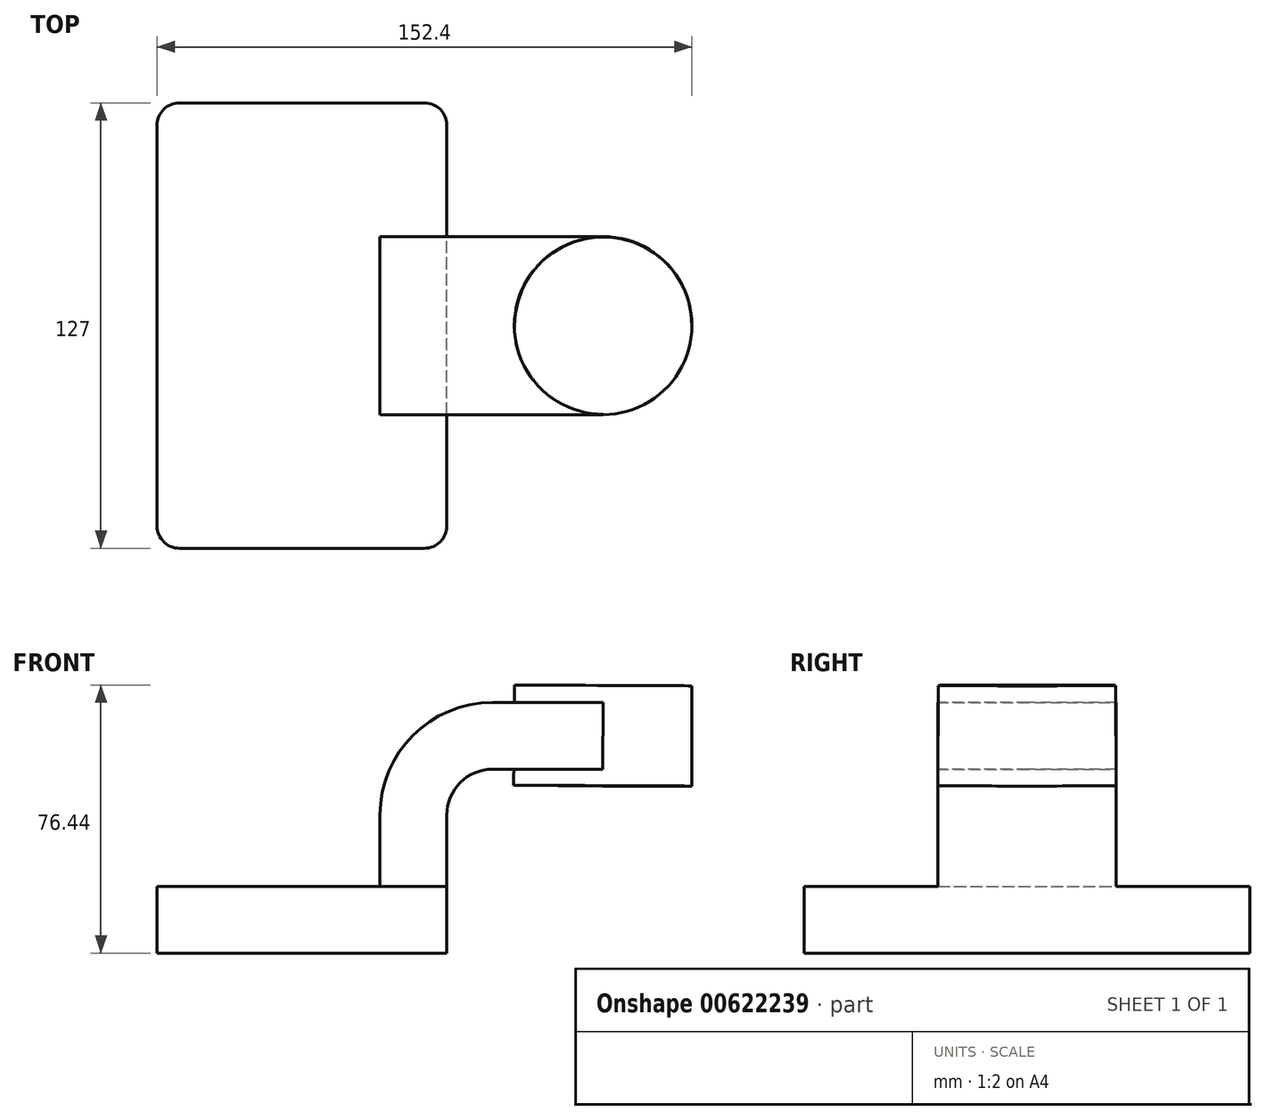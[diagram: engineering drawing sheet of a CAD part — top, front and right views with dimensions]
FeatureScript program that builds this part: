
annotation { "Feature Type Name" : "Feature", "Feature Type Description" : "" }
export const myFeature = defineFeature(function(context is Context, id is Id, definition is map)
    precondition{}
    {
        {
            var Q0;
            Q0=qCreatedBy(makeId("Front.planeOp"),FACE);
            var sketch = newSketch(context, id + "F0", { "sketchPlane" : qUnion([Q0])});
            skLineSegment(sketch, "E0.bottom", {"start": v(41.27, 9.53) * mm, "end": v(-41.28, 9.53) * mm});
            skLineSegment(sketch, "E0.top", {"start": v(41.28, -9.52) * mm, "end": v(-41.27, -9.52) * mm});
            skLineSegment(sketch, "E0.left", {"start": v(41.28, 9.53) * mm, "end": v(41.28, -9.52) * mm});
            skLineSegment(sketch, "E0.right", {"start": v(-41.28, 9.53) * mm, "end": v(-41.27, -9.52) * mm});
            skPoint(sketch, "E0.middle", {"position": v(0, 0) * mm});
            skLineSegment(sketch, "E1.bottom", {"start": v(111.12, 66.68) * mm, "end": v(60.32, 66.68) * mm});
            skLineSegment(sketch, "E1.top", {"start": v(111.12, 38.1) * mm, "end": v(60.32, 38.1) * mm});
            skLineSegment(sketch, "E1.left", {"start": v(111.12, 66.68) * mm, "end": v(111.12, 38.1) * mm});
            skLineSegment(sketch, "E1.right", {"start": v(60.32, 66.68) * mm, "end": v(60.32, 38.1) * mm});
            skPoint(sketch, "E1.middle", {"position": v(85.72, 52.39) * mm});
            skLineSegment(sketch, "E2", {"start": v(41.27, 9.53) * mm, "end": v(41.27, 29.84) * mm});
            skArc(sketch, "E3", {"start": v(41.27, 29.84) * mm, "mid": v(45.1, 39.06) * mm, "end": v(54.31, 42.88) * mm});
            skLineSegment(sketch, "E4", {"start": v(54.31, 42.88) * mm, "end": v(85.86, 42.88) * mm});
            skLineSegment(sketch, "E5.0", {"start": v(54.31, 61.93) * mm, "end": v(85.86, 61.93) * mm});
            skArc(sketch, "E5.1", {"start": v(22.22, 29.84) * mm, "mid": v(31.62, 52.53) * mm, "end": v(54.31, 61.93) * mm});
            skLineSegment(sketch, "E5.2", {"start": v(22.22, 9.53) * mm, "end": v(22.22, 29.84) * mm});
            skLineSegment(sketch, "E6", {"start": v(85.72, 38.1) * mm, "end": v(85.86, 66.68) * mm});
            skFitSpline(sketch, "E7", {"points": [v(-41.28, 9.52) * mm, v(54.31, 61.93) * mm], "startDerivative": vector(4.7, 92.75) * mm, "endDerivative": vector(132.26, -2.13) * mm});
            skSolve(sketch);
        }
        {
            var Q0;
            Q0=makeQuery(id+"F0.imprint","IMPRINT",FACE,{"disambiguationData":[TD([[makeQuery(id+"F0.imprint","IMPRINT",EDGE,{"derivedFrom":sQuery(id+"F0.wireOp",EDGE,"E0.top")}),-1.0]])]});
            extrude(context, id + "F1", {"entities" : qUnion([Q0]), "endBound" : BoundingType.SYMMETRIC, "depth" : 127 * mm, "offsetDistance" : 25.4 * mm});
        }
        {
            var Q0;
            {var subQ1=sQuery(id+"F0.wireOp",EDGE,"E2");Q0=makeQuery(id+"F0.imprint","IMPRINT",FACE,{"disambiguationData":[TD([[makeQuery(id+"F0.imprint","IMPRINT",EDGE,{"derivedFrom":subQ1}),1.0]])]});}
            var Q1;
            {var subQ0=sQuery(id+"F0.wireOp",EDGE,"E5.0");var subQ1=sQuery(id+"F0.wireOp",EDGE,"E1.right");var subQ2=makeQuery(id+"F0.imprint","INTERSECT",VERTEX,{"derivedFrom":[subQ1,subQ0]});Q1=makeQuery(id+"F0.imprint","IMPRINT",FACE,{"disambiguationData":[TD([[makeQuery(id+"F0.imprint","IMPRINT",EDGE,{"disambiguationData":[TD([[subQ2,-1.0]])],"derivedFrom":subQ1}),1.0]])]});}
            extrude(context, id + "F2", {"entities" : qUnion([Q0, Q1]), "operationType" : NewBodyOperationType.ADD, "endBound" : BoundingType.SYMMETRIC, "depth" : 50.8 * mm, "offsetDistance" : 25.4 * mm});
        }
        {
            var Q0;
            Q0=makeQuery(id+"F0.imprint","IMPRINT",FACE,{"disambiguationData":[TD([[makeQuery(id+"F0.imprint","IMPRINT",EDGE,{"derivedFrom":sQuery(id+"F0.wireOp",EDGE,"E5.1")}),1.0]])]});
            extrude(context, id + "F3", {"entities" : qUnion([Q0]), "operationType" : NewBodyOperationType.ADD, "endBound" : BoundingType.SYMMETRIC, "depth" : 15.88 * mm, "offsetDistance" : 25.4 * mm});
        }
        {
            var Q0;
            {var subQ4=sQuery(id+"F0.wireOp",EDGE,"E1.left");Q0=makeQuery(id+"F0.imprint","IMPRINT",FACE,{"disambiguationData":[TD([[makeQuery(id+"F0.imprint","IMPRINT",EDGE,{"derivedFrom":subQ4}),-1.0]])]});}
            var Q1;
            Q1=sQuery(id+"F0.wireOp",EDGE,"E6");
            revolve(context, id + "F4", {"operationType" : NewBodyOperationType.ADD, "entities" : qUnion([Q0]), "axis" : qUnion([Q1]), "revolveType" : RevolveType.FULL});
        }
        {
            var Q0;
            Q0=makeQuery(id+"F1.opExtrude","CAP_EDGE",EDGE,{"disambiguationData":[OSD([sQuery(id+"F0.wireOp",EDGE,"E0.right")])],"isStart":false});
            var Q1;
            Q1=makeQuery(id+"F1.opExtrude","CAP_EDGE",EDGE,{"disambiguationData":[OSD([sQuery(id+"F0.wireOp",EDGE,"E0.left")])],"isStart":false});
            var Q2;
            Q2=makeQuery(id+"F1.opExtrude","CAP_EDGE",EDGE,{"disambiguationData":[OSD([sQuery(id+"F0.wireOp",EDGE,"E0.left")])],"isStart":true});
            var Q3;
            Q3=makeQuery(id+"F1.opExtrude","CAP_EDGE",EDGE,{"disambiguationData":[OSD([sQuery(id+"F0.wireOp",EDGE,"E0.right")])],"isStart":true});
            fillet(context, id + "F5", {"entities" : qUnion([Q0, Q1, Q2, Q3]), "radius" : 6.35 * mm, "tangentPropagation" : true, "allowEdgeOverflow" : false});
        }
    });
